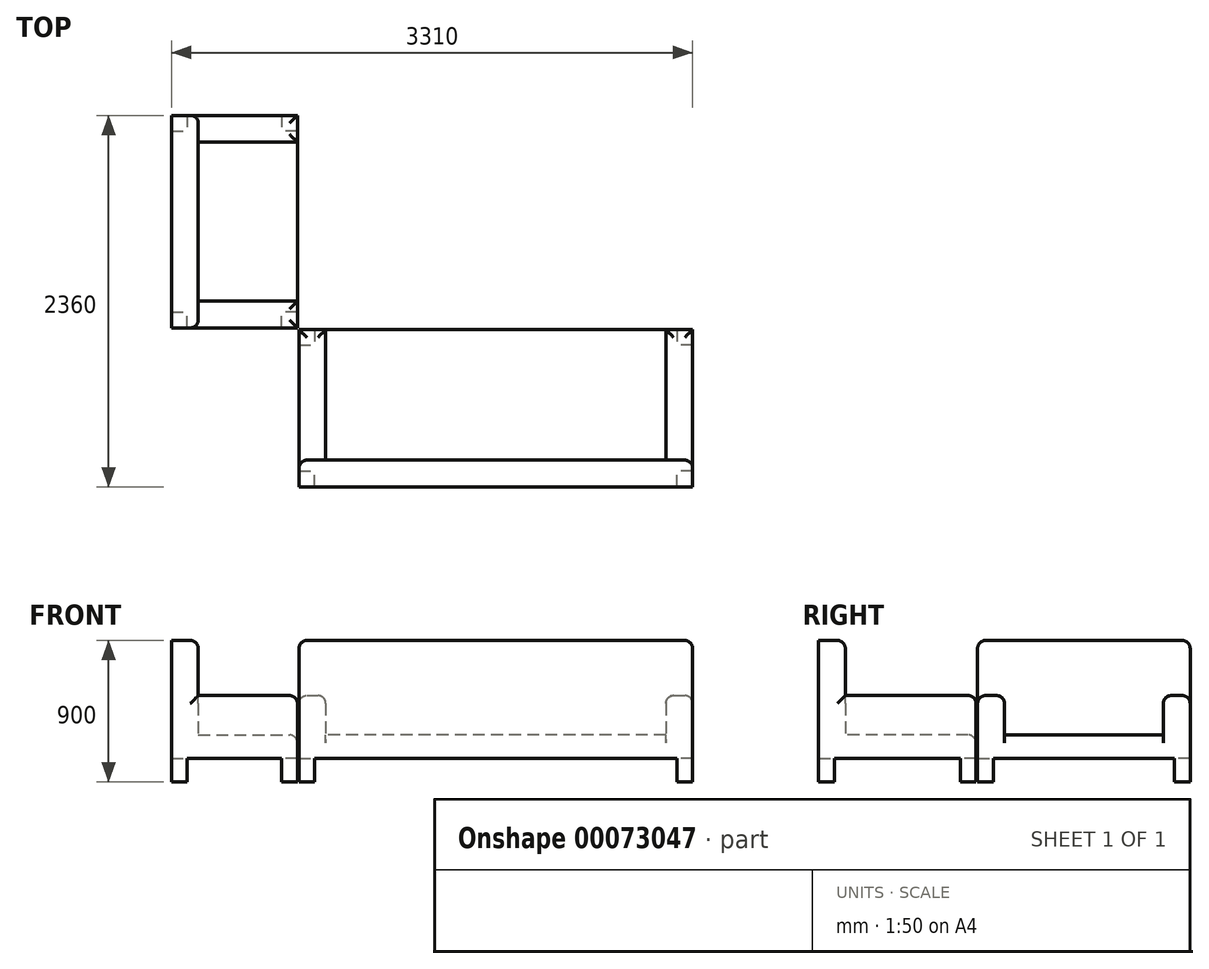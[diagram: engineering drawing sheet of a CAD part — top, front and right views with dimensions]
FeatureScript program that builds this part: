
annotation { "Feature Type Name" : "Feature", "Feature Type Description" : "" }
export const myFeature = defineFeature(function(context is Context, id is Id, definition is map)
    precondition{}
    {
        {
            var Q0;
            Q0=qCreatedBy(makeId("Top.planeOp"),FACE);
            var sketch = newSketch(context, id + "F0", { "sketchPlane" : qUnion([Q0])});
            skLineSegment(sketch, "E0.bottom", {"start": v(1250, -500) * mm, "end": v(-1250, -500) * mm});
            skLineSegment(sketch, "E0.top", {"start": v(1250, 500) * mm, "end": v(-1250, 500) * mm});
            skLineSegment(sketch, "E0.left", {"start": v(1250, -500) * mm, "end": v(1250, 500) * mm});
            skLineSegment(sketch, "E0.right", {"start": v(-1250, -500) * mm, "end": v(-1250, 500) * mm});
            skPoint(sketch, "E0.middle", {"position": v(0, 0) * mm});
            skSolve(sketch);
        }
        {
            var Q0;
            Q0=makeQuery(id+"F0.imprint","IMPRINT",FACE,{"disambiguationData":[TD([[makeQuery(id+"F0.imprint","IMPRINT",EDGE,{"derivedFrom":sQuery(id+"F0.wireOp",EDGE,"E0.bottom")}),-1.0]])]});
            extrude(context, id + "F1", {"entities" : qUnion([Q0]), "depth" : 150 * mm});
        }
        {
            var Q0;
            Q0=makeQuery(id+"F1.opExtrude","CAP_FACE",FACE,{"disambiguationData":[OSD([sQuery(id+"F0.wireOp",EDGE,"E0.bottom"),sQuery(id+"F0.wireOp",EDGE,"E0.top"),sQuery(id+"F0.wireOp",EDGE,"E0.left"),sQuery(id+"F0.wireOp",EDGE,"E0.right")])],"isStart":false});
            var sketch = newSketch(context, id + "F2", { "sketchPlane" : qUnion([Q0])});
            skLineSegment(sketch, "E1.bottom", {"start": v(-1250, -500) * mm, "end": v(1250, -500) * mm});
            skLineSegment(sketch, "E1.top", {"start": v(-1250, -330) * mm, "end": v(1250, -330) * mm});
            skLineSegment(sketch, "E1.left", {"start": v(-1250, -330) * mm, "end": v(-1250, -500) * mm});
            skLineSegment(sketch, "E1.right", {"start": v(1250, -330) * mm, "end": v(1250, -500) * mm});
            skPoint(sketch, "E1.middle", {"position": v(0, -415) * mm});
            skLineSegment(sketch, "E2.bottom", {"start": v(1250, 500) * mm, "end": v(1080, 500) * mm});
            skLineSegment(sketch, "E2.top", {"start": v(1250, -330) * mm, "end": v(1080, -330) * mm});
            skLineSegment(sketch, "E2.left", {"start": v(1250, 500) * mm, "end": v(1250, -330) * mm});
            skLineSegment(sketch, "E2.right", {"start": v(1080, 500) * mm, "end": v(1080, -330) * mm});
            skLineSegment(sketch, "E3.bottom", {"start": v(-1250, 500) * mm, "end": v(-1080, 500) * mm});
            skLineSegment(sketch, "E3.top", {"start": v(-1250, -330) * mm, "end": v(-1080, -330) * mm});
            skLineSegment(sketch, "E3.left", {"start": v(-1250, 500) * mm, "end": v(-1250, -330) * mm});
            skLineSegment(sketch, "E3.right", {"start": v(-1080, 500) * mm, "end": v(-1080, -330) * mm});
            skSolve(sketch);
        }
        {
            var Q0;
            Q0=makeQuery(id+"F2.imprint","IMPRINT",FACE,{"disambiguationData":[TD([[makeQuery(id+"F2.imprint","IMPRINT",EDGE,{"derivedFrom":sQuery(id+"F2.wireOp",EDGE,"E1.bottom")}),-1.0]])]});
            extrude(context, id + "F3", {"entities" : qUnion([Q0]), "operationType" : NewBodyOperationType.ADD, "depth" : 600 * mm});
        }
        {
            var Q0;
            Q0=makeQuery(id+"F2.imprint","IMPRINT",FACE,{"disambiguationData":[TD([[makeQuery(id+"F2.imprint","IMPRINT",EDGE,{"derivedFrom":sQuery(id+"F2.wireOp",EDGE,"E3.bottom")}),1.0]])]});
            var Q1;
            Q1=makeQuery(id+"F2.imprint","IMPRINT",FACE,{"disambiguationData":[TD([[makeQuery(id+"F2.imprint","IMPRINT",EDGE,{"derivedFrom":sQuery(id+"F2.wireOp",EDGE,"E2.bottom")}),1.0]])]});
            extrude(context, id + "F4", {"entities" : qUnion([Q0, Q1]), "operationType" : NewBodyOperationType.ADD, "depth" : 250 * mm});
        }
        {
            var Q0;
            Q0=makeQuery(id+"F4.opExtrude","CAP_EDGE",EDGE,{"disambiguationData":[OSD([sQuery(id+"F2.wireOp",EDGE,"E3.right")])],"isStart":false});
            var Q1;
            Q1=makeQuery(id+"F4.opExtrude","CAP_EDGE",EDGE,{"disambiguationData":[OSD([sQuery(id+"F2.wireOp",EDGE,"E3.bottom")])],"isStart":false});
            var Q2;
            Q2=makeQuery(id+"F4.opExtrude","CAP_EDGE",EDGE,{"disambiguationData":[OSD([sQuery(id+"F2.wireOp",EDGE,"E3.left")])],"isStart":false});
            var Q3;
            Q3=makeQuery(id+"F4.opExtrude","CAP_EDGE",EDGE,{"disambiguationData":[OSD([sQuery(id+"F2.wireOp",EDGE,"E2.right")])],"isStart":false});
            var Q4;
            Q4=makeQuery(id+"F4.opExtrude","CAP_EDGE",EDGE,{"disambiguationData":[OSD([sQuery(id+"F2.wireOp",EDGE,"E2.left")])],"isStart":false});
            var Q5;
            Q5=makeQuery(id+"F4.opExtrude","CAP_EDGE",EDGE,{"disambiguationData":[OSD([sQuery(id+"F2.wireOp",EDGE,"E2.bottom")])],"isStart":false});
            var Q6;
            Q6=makeQuery(id+"F1.opExtrude","CAP_EDGE",EDGE,{"disambiguationData":[OSD([sQuery(id+"F0.wireOp",EDGE,"E0.top")])],"isStart":false});
            var Q7;
            Q7=makeQuery(id+"F3.opExtrude","SWEPT_EDGE",EDGE,{"disambiguationData":[OSD([sQuery(id+"F2.wireOp",EDGE,"E1.left"),sQuery(id+"F2.wireOp",EDGE,"E3.top"),sQuery(id+"F2.wireOp",EDGE,"E3.left")])]});
            var Q8;
            Q8=makeQuery(id+"F3.opExtrude","CAP_EDGE",EDGE,{"disambiguationData":[OSD([sQuery(id+"F2.wireOp",EDGE,"E1.top"),sQuery(id+"F2.wireOp",EDGE,"E2.top"),sQuery(id+"F2.wireOp",EDGE,"E3.top")])],"isStart":false});
            var Q9;
            Q9=makeQuery(id+"F3.opExtrude","CAP_EDGE",EDGE,{"disambiguationData":[OSD([sQuery(id+"F2.wireOp",EDGE,"E1.left")])],"isStart":false});
            var Q10;
            Q10=makeQuery(id+"F3.opExtrude","SWEPT_EDGE",EDGE,{"disambiguationData":[OSD([sQuery(id+"F2.wireOp",EDGE,"E1.right"),sQuery(id+"F2.wireOp",EDGE,"E2.top"),sQuery(id+"F2.wireOp",EDGE,"E2.left")])]});
            var Q11;
            Q11=makeQuery(id+"F3.opExtrude","CAP_EDGE",EDGE,{"disambiguationData":[OSD([sQuery(id+"F2.wireOp",EDGE,"E1.right")])],"isStart":false});
            fillet(context, id + "F5", {"entities" : qUnion([Q0, Q1, Q2, Q3, Q4, Q5, Q6, Q7, Q8, Q9, Q10, Q11]), "radius" : 50 * mm, "tangentPropagation" : true, "allowEdgeOverflow" : false});
        }
        {
            var Q0;
            Q0=makeQuery(id+"F1.opExtrude","CAP_FACE",FACE,{"disambiguationData":[OSD([sQuery(id+"F0.wireOp",EDGE,"E0.bottom"),sQuery(id+"F0.wireOp",EDGE,"E0.top"),sQuery(id+"F0.wireOp",EDGE,"E0.left"),sQuery(id+"F0.wireOp",EDGE,"E0.right")])],"isStart":true});
            var sketch = newSketch(context, id + "F6", { "sketchPlane" : qUnion([Q0])});
            skLineSegment(sketch, "E4.bottom", {"start": v(1250, -500) * mm, "end": v(1150, -500) * mm});
            skLineSegment(sketch, "E4.top", {"start": v(1250, -400) * mm, "end": v(1150, -400) * mm});
            skLineSegment(sketch, "E4.left", {"start": v(1250, -500) * mm, "end": v(1250, -400) * mm});
            skLineSegment(sketch, "E4.right", {"start": v(1150, -500) * mm, "end": v(1150, -400) * mm});
            skLineSegment(sketch, "E5.MirrorCS", {"start": v(-1250, -400) * mm, "end": v(-1150, -400) * mm});
            skLineSegment(sketch, "E6.MirrorCS", {"start": v(-1250, -500) * mm, "end": v(-1250, -400) * mm});
            skLineSegment(sketch, "E7.MirrorCS", {"start": v(-1250, -500) * mm, "end": v(-1150, -500) * mm});
            skLineSegment(sketch, "E8.MirrorCS", {"start": v(-1150, -500) * mm, "end": v(-1150, -400) * mm});
            skLineSegment(sketch, "E9.MirrorCS", {"start": v(1250, 400) * mm, "end": v(1150, 400) * mm});
            skLineSegment(sketch, "E10.MirrorCS", {"start": v(1150, 500) * mm, "end": v(1150, 400) * mm});
            skLineSegment(sketch, "E11.MirrorCS", {"start": v(1250, 500) * mm, "end": v(1250, 400) * mm});
            skLineSegment(sketch, "E12.MirrorCS", {"start": v(1250, 500) * mm, "end": v(1150, 500) * mm});
            skLineSegment(sketch, "E13.MirrorCS", {"start": v(-1150, 500) * mm, "end": v(-1150, 400) * mm});
            skLineSegment(sketch, "E14.MirrorCS", {"start": v(-1250, 500) * mm, "end": v(-1150, 500) * mm});
            skLineSegment(sketch, "E15.MirrorCS", {"start": v(-1250, 400) * mm, "end": v(-1150, 400) * mm});
            skLineSegment(sketch, "E16.MirrorCS", {"start": v(-1250, 500) * mm, "end": v(-1250, 400) * mm});
            skSolve(sketch);
        }
        {
            var Q0;
            Q0=makeQuery(id+"F6.imprint","IMPRINT",FACE,{"disambiguationData":[TD([[makeQuery(id+"F6.imprint","IMPRINT",EDGE,{"derivedFrom":sQuery(id+"F6.wireOp",EDGE,"E9.MirrorCS")}),-1.0]])]});
            var Q1;
            Q1=makeQuery(id+"F6.imprint","IMPRINT",FACE,{"disambiguationData":[TD([[makeQuery(id+"F6.imprint","IMPRINT",EDGE,{"derivedFrom":sQuery(id+"F6.wireOp",EDGE,"E4.bottom")}),-1.0]])]});
            var Q2;
            Q2=makeQuery(id+"F6.imprint","IMPRINT",FACE,{"disambiguationData":[TD([[makeQuery(id+"F6.imprint","IMPRINT",EDGE,{"derivedFrom":sQuery(id+"F6.wireOp",EDGE,"E5.MirrorCS")}),-1.0]])]});
            var Q3;
            Q3=makeQuery(id+"F6.imprint","IMPRINT",FACE,{"disambiguationData":[TD([[makeQuery(id+"F6.imprint","IMPRINT",EDGE,{"derivedFrom":sQuery(id+"F6.wireOp",EDGE,"E13.MirrorCS")}),-1.0]])]});
            extrude(context, id + "F7", {"entities" : qUnion([Q0, Q1, Q2, Q3]), "operationType" : NewBodyOperationType.ADD, "depth" : 150 * mm});
        }
        {
            var Q0;
            Q0=qCreatedBy(makeId("Top.planeOp"),FACE);
            var sketch = newSketch(context, id + "F8", { "sketchPlane" : qUnion([Q0])});
            skLineSegment(sketch, "E17.bottom", {"start": v(-1260, 510) * mm, "end": v(-2060, 510) * mm});
            skLineSegment(sketch, "E17.top", {"start": v(-1260, 1860) * mm, "end": v(-2060, 1860) * mm});
            skLineSegment(sketch, "E17.left", {"start": v(-1260, 510) * mm, "end": v(-1260, 1860) * mm});
            skLineSegment(sketch, "E17.right", {"start": v(-2060, 510) * mm, "end": v(-2060, 1860) * mm});
            skPoint(sketch, "E17.middle", {"position": v(-1660, 1185) * mm});
            skSolve(sketch);
        }
        {
            var Q0;
            Q0=makeQuery(id+"F8.imprint","IMPRINT",FACE,{"disambiguationData":[TD([[makeQuery(id+"F8.imprint","IMPRINT",EDGE,{"derivedFrom":sQuery(id+"F8.wireOp",EDGE,"E17.bottom")}),-1.0]])]});
            var Q1;
            Q1=makeQuery(id+"F1.opExtrude","CAP_FACE",FACE,{"disambiguationData":[OSD([sQuery(id+"F0.wireOp",EDGE,"E0.bottom"),sQuery(id+"F0.wireOp",EDGE,"E0.top"),sQuery(id+"F0.wireOp",EDGE,"E0.left"),sQuery(id+"F0.wireOp",EDGE,"E0.right")])],"isStart":false});
            extrude(context, id + "F9", {"entities" : qUnion([Q0]), "endBound" : BoundingType.UP_TO_SURFACE, "endBoundEntityFace" : qUnion([Q1]), "depth" : 25 * mm});
        }
        {
            var Q0;
            Q0=makeQuery(id+"F9.opExtrude","CAP_FACE",FACE,{"disambiguationData":[OSD([sQuery(id+"F8.wireOp",EDGE,"E17.bottom"),sQuery(id+"F8.wireOp",EDGE,"E17.top"),sQuery(id+"F8.wireOp",EDGE,"E17.left"),sQuery(id+"F8.wireOp",EDGE,"E17.right")])],"isStart":false});
            var sketch = newSketch(context, id + "F10", { "sketchPlane" : qUnion([Q0])});
            skLineSegment(sketch, "E18", {"start": v(-1260, 510) * mm, "end": v(-2060, 510) * mm});
            skLineSegment(sketch, "E19", {"start": v(-2060, 510) * mm, "end": v(-2060, 1860) * mm});
            skLineSegment(sketch, "E20", {"start": v(-2060, 1860) * mm, "end": v(-1890, 1860) * mm});
            skLineSegment(sketch, "E21", {"start": v(-1890, 1860) * mm, "end": v(-1890, 680) * mm});
            skLineSegment(sketch, "E22", {"start": v(-1890, 680) * mm, "end": v(-1260, 680) * mm});
            skLineSegment(sketch, "E23", {"start": v(-1260, 680) * mm, "end": v(-1260, 510) * mm});
            skLineSegment(sketch, "E24", {"start": v(-1890, 680) * mm, "end": v(-1890, 510) * mm});
            skLineSegment(sketch, "E25.bottom", {"start": v(-1260, 1860) * mm, "end": v(-2340, 1860) * mm});
            skLineSegment(sketch, "E25.top", {"start": v(-1260, 1690) * mm, "end": v(-1890, 1690) * mm});
            skLineSegment(sketch, "E25.left", {"start": v(-1260, 1860) * mm, "end": v(-1260, 1690) * mm});
            skSolve(sketch);
        }
        {
            var Q0;
            Q0=makeQuery(id+"F10.imprint","IMPRINT",FACE,{"disambiguationData":[TD([[makeQuery(id+"F10.imprint","IMPRINT",EDGE,{"derivedFrom":sQuery(id+"F10.wireOp",EDGE,"E22")}),-1.0]])]});
            var Q1;
            {var subQ0=sQuery(id+"F10.wireOp",EDGE,"E25.bottom");Q1=makeQuery(id+"F10.imprint","IMPRINT",FACE,{"disambiguationData":[TD([[makeQuery(id+"F10.imprint","IMPRINT",EDGE,{"derivedFrom":subQ0}),1.0]])]});}
            var Q2;
            Q2=makeQuery(id+"F4.opExtrude","CAP_FACE",FACE,{"disambiguationData":[OSD([sQuery(id+"F2.wireOp",EDGE,"E3.bottom"),sQuery(id+"F2.wireOp",EDGE,"E3.top"),sQuery(id+"F2.wireOp",EDGE,"E3.left"),sQuery(id+"F2.wireOp",EDGE,"E3.right")])],"isStart":false});
            extrude(context, id + "F11", {"entities" : qUnion([Q0, Q1]), "operationType" : NewBodyOperationType.ADD, "endBound" : BoundingType.UP_TO_SURFACE, "endBoundEntityFace" : qUnion([Q2]), "depth" : 25 * mm});
        }
        {
            var Q0;
            {var subQ1=sQuery(id+"F10.wireOp",EDGE,"E19");Q0=makeQuery(id+"F10.imprint","IMPRINT",FACE,{"disambiguationData":[TD([[makeQuery(id+"F10.imprint","IMPRINT",EDGE,{"derivedFrom":subQ1}),-1.0]])]});}
            var Q1;
            Q1=makeQuery(id+"F3.opExtrude","CAP_FACE",FACE,{"disambiguationData":[OSD([sQuery(id+"F2.wireOp",EDGE,"E1.bottom"),sQuery(id+"F2.wireOp",EDGE,"E1.top"),sQuery(id+"F2.wireOp",EDGE,"E1.left"),sQuery(id+"F2.wireOp",EDGE,"E1.right"),sQuery(id+"F2.wireOp",EDGE,"E2.top"),sQuery(id+"F2.wireOp",EDGE,"E3.top")])],"isStart":false});
            extrude(context, id + "F12", {"entities" : qUnion([Q0]), "operationType" : NewBodyOperationType.ADD, "endBound" : BoundingType.UP_TO_SURFACE, "endBoundEntityFace" : qUnion([Q1]), "depth" : 25 * mm});
        }
        {
            var Q0;
            Q0=makeQuery(id+"F11.opExtrude","CAP_EDGE",EDGE,{"disambiguationData":[OSD([sQuery(id+"F10.wireOp",EDGE,"E22")])],"isStart":false});
            var Q1;
            Q1=makeQuery(id+"F11.opExtrude","CAP_EDGE",EDGE,{"disambiguationData":[OSD([sQuery(id+"F10.wireOp",EDGE,"E18")])],"isStart":false});
            var Q2;
            Q2=makeQuery(id+"F11.opExtrude","CAP_EDGE",EDGE,{"disambiguationData":[OSD([sQuery(id+"F10.wireOp",EDGE,"E23")])],"isStart":false});
            var Q3;
            Q3=makeQuery(id+"F9.opExtrude","CAP_EDGE",EDGE,{"disambiguationData":[OSD([sQuery(id+"F8.wireOp",EDGE,"E17.left")])],"isStart":false});
            var Q4;
            Q4=makeQuery(id+"F12.opExtrude","CAP_EDGE",EDGE,{"disambiguationData":[OSD([sQuery(id+"F10.wireOp",EDGE,"E18")])],"isStart":false});
            var Q5;
            Q5=makeQuery(id+"F12.opExtrude","CAP_EDGE",EDGE,{"disambiguationData":[OSD([sQuery(id+"F10.wireOp",EDGE,"E21"),sQuery(id+"F10.wireOp",EDGE,"E24")])],"isStart":false});
            var Q6;
            Q6=makeQuery(id+"F12.opExtrude","SWEPT_EDGE",EDGE,{"disambiguationData":[OSD([sQuery(id+"F10.wireOp",EDGE,"E18"),sQuery(id+"F10.wireOp",EDGE,"E24")])]});
            var Q7;
            Q7=makeQuery(id+"F11.opExtrude","CAP_EDGE",EDGE,{"disambiguationData":[OSD([sQuery(id+"F10.wireOp",EDGE,"E25.left")])],"isStart":false});
            var Q8;
            Q8=makeQuery(id+"F11.opExtrude","CAP_EDGE",EDGE,{"disambiguationData":[OSD([sQuery(id+"F10.wireOp",EDGE,"E25.bottom")])],"isStart":false});
            var Q9;
            Q9=makeQuery(id+"F11.opExtrude","CAP_EDGE",EDGE,{"disambiguationData":[OSD([sQuery(id+"F10.wireOp",EDGE,"E25.top")])],"isStart":false});
            var Q10;
            Q10=makeQuery(id+"F12.opExtrude","SWEPT_EDGE",EDGE,{"disambiguationData":[OSD([sQuery(id+"F10.wireOp",EDGE,"E20"),sQuery(id+"F10.wireOp",EDGE,"E21"),sQuery(id+"F10.wireOp",EDGE,"E25.bottom")])]});
            var Q11;
            Q11=makeQuery(id+"F12.opExtrude","CAP_EDGE",EDGE,{"disambiguationData":[OSD([sQuery(id+"F10.wireOp",EDGE,"E20")])],"isStart":false});
            fillet(context, id + "F13", {"entities" : qUnion([Q0, Q1, Q2, Q3, Q4, Q5, Q6, Q7, Q8, Q9, Q10, Q11]), "radius" : 50 * mm, "tangentPropagation" : true, "allowEdgeOverflow" : false});
        }
        {
            var Q0;
            Q0=makeQuery(id+"F9.opExtrude","CAP_FACE",FACE,{"disambiguationData":[OSD([sQuery(id+"F8.wireOp",EDGE,"E17.bottom"),sQuery(id+"F8.wireOp",EDGE,"E17.top"),sQuery(id+"F8.wireOp",EDGE,"E17.left"),sQuery(id+"F8.wireOp",EDGE,"E17.right")])],"isStart":true});
            var sketch = newSketch(context, id + "F14", { "sketchPlane" : qUnion([Q0])});
            skLineSegment(sketch, "E26", {"start": v(-2060, -1185) * mm, "end": v(-1260, -1185) * mm, "construction": true});
            skLineSegment(sketch, "E27", {"start": v(-1660, -1860) * mm, "end": v(-1660, -510) * mm, "construction": true});
            skLineSegment(sketch, "E28.bottom", {"start": v(-2060, -1860) * mm, "end": v(-1960, -1860) * mm});
            skLineSegment(sketch, "E28.top", {"start": v(-2060, -1760) * mm, "end": v(-1960, -1760) * mm});
            skLineSegment(sketch, "E28.left", {"start": v(-2060, -1860) * mm, "end": v(-2060, -1760) * mm});
            skLineSegment(sketch, "E28.right", {"start": v(-1960, -1860) * mm, "end": v(-1960, -1760) * mm});
            skLineSegment(sketch, "E29.MirrorCS", {"start": v(-1960, -510) * mm, "end": v(-1960, -610) * mm});
            skLineSegment(sketch, "E30.MirrorCS", {"start": v(-2060, -510) * mm, "end": v(-2060, -610) * mm});
            skLineSegment(sketch, "E31.MirrorCS", {"start": v(-2060, -510) * mm, "end": v(-1960, -510) * mm});
            skLineSegment(sketch, "E32.MirrorCS", {"start": v(-2060, -610) * mm, "end": v(-1960, -610) * mm});
            skLineSegment(sketch, "E33.MirrorCS", {"start": v(-1260, -610) * mm, "end": v(-1360, -610) * mm});
            skLineSegment(sketch, "E34.MirrorCS", {"start": v(-1260, -510) * mm, "end": v(-1360, -510) * mm});
            skLineSegment(sketch, "E35.MirrorCS", {"start": v(-1260, -510) * mm, "end": v(-1260, -610) * mm});
            skLineSegment(sketch, "E36.MirrorCS", {"start": v(-1360, -510) * mm, "end": v(-1360, -610) * mm});
            skLineSegment(sketch, "E37.MirrorCS", {"start": v(-1260, -1860) * mm, "end": v(-1360, -1860) * mm});
            skLineSegment(sketch, "E38.MirrorCS", {"start": v(-1260, -1760) * mm, "end": v(-1360, -1760) * mm});
            skLineSegment(sketch, "E39.MirrorCS", {"start": v(-1360, -1860) * mm, "end": v(-1360, -1760) * mm});
            skLineSegment(sketch, "E40.MirrorCS", {"start": v(-1260, -1860) * mm, "end": v(-1260, -1760) * mm});
            skSolve(sketch);
        }
        {
            var Q0;
            Q0=makeQuery(id+"F14.imprint","IMPRINT",FACE,{"disambiguationData":[TD([[makeQuery(id+"F14.imprint","IMPRINT",EDGE,{"derivedFrom":sQuery(id+"F14.wireOp",EDGE,"E28.bottom")}),-1.0]])]});
            var Q1;
            Q1=makeQuery(id+"F14.imprint","IMPRINT",FACE,{"disambiguationData":[TD([[makeQuery(id+"F14.imprint","IMPRINT",EDGE,{"derivedFrom":sQuery(id+"F14.wireOp",EDGE,"E37.MirrorCS")}),-1.0]])]});
            var Q2;
            Q2=makeQuery(id+"F14.imprint","IMPRINT",FACE,{"disambiguationData":[TD([[makeQuery(id+"F14.imprint","IMPRINT",EDGE,{"derivedFrom":sQuery(id+"F14.wireOp",EDGE,"E33.MirrorCS")}),-1.0]])]});
            var Q3;
            Q3=makeQuery(id+"F14.imprint","IMPRINT",FACE,{"disambiguationData":[TD([[makeQuery(id+"F14.imprint","IMPRINT",EDGE,{"derivedFrom":sQuery(id+"F14.wireOp",EDGE,"E29.MirrorCS")}),-1.0]])]});
            var Q4;
            Q4=makeQuery(id+"F7.opExtrude","CAP_FACE",FACE,{"disambiguationData":[OSD([sQuery(id+"F6.wireOp",EDGE,"E5.MirrorCS"),sQuery(id+"F6.wireOp",EDGE,"E6.MirrorCS"),sQuery(id+"F6.wireOp",EDGE,"E7.MirrorCS"),sQuery(id+"F6.wireOp",EDGE,"E8.MirrorCS")])],"isStart":false});
            extrude(context, id + "F15", {"entities" : qUnion([Q0, Q1, Q2, Q3]), "operationType" : NewBodyOperationType.ADD, "endBound" : BoundingType.UP_TO_SURFACE, "endBoundEntityFace" : qUnion([Q4]), "depth" : 25 * mm});
        }
    });
